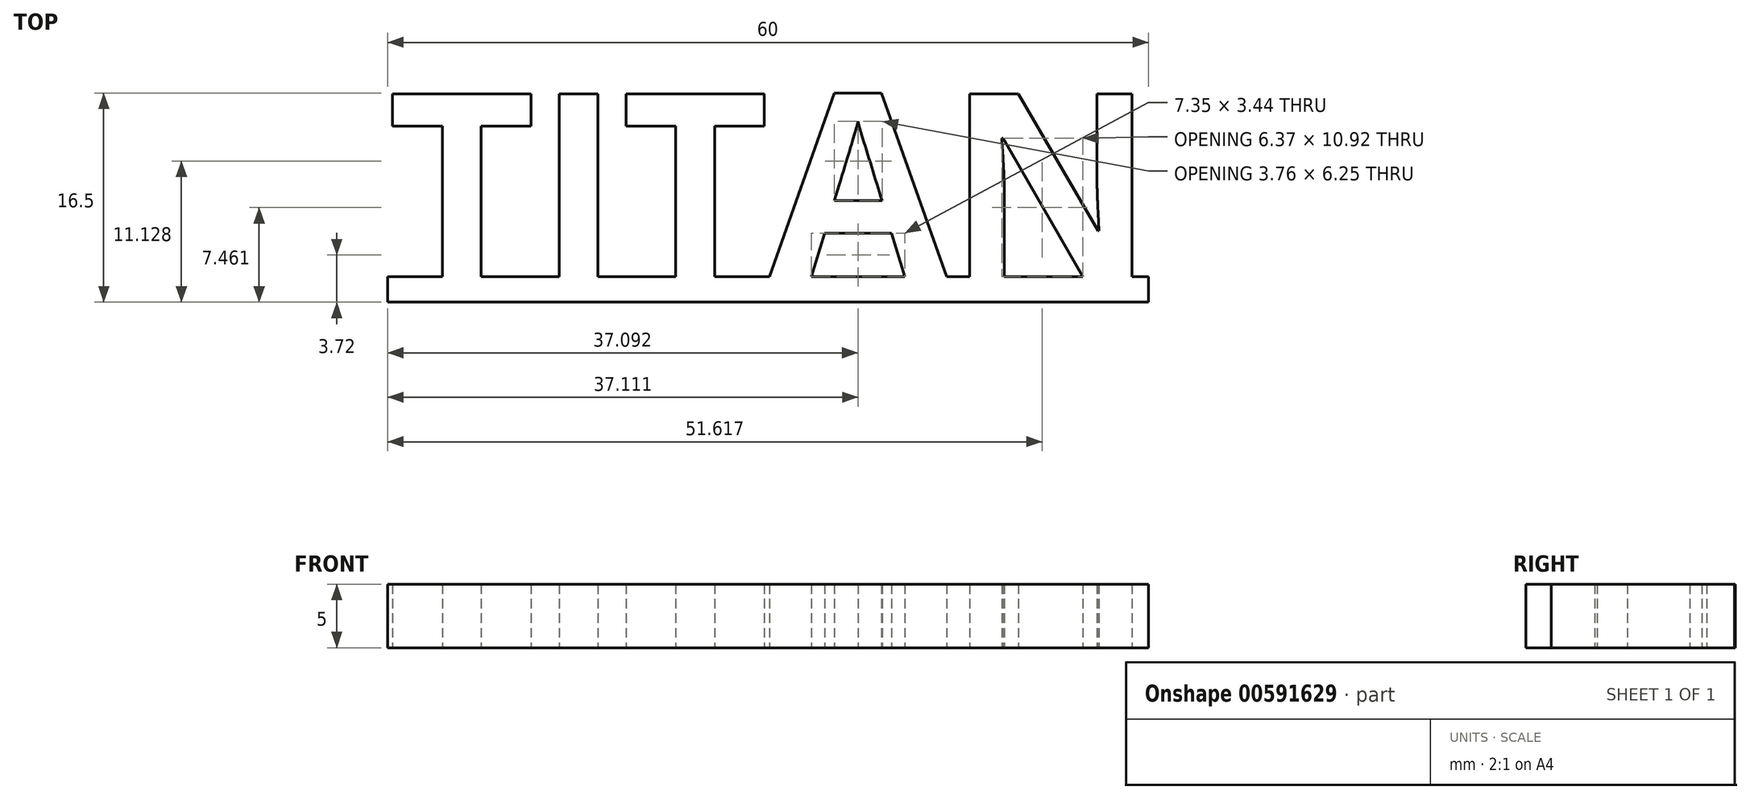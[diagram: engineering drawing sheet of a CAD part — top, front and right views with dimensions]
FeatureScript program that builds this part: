
annotation { "Feature Type Name" : "Feature", "Feature Type Description" : "" }
export const myFeature = defineFeature(function(context is Context, id is Id, definition is map)
    precondition{}
    {
        {
            var Q0;
            Q0=qCreatedBy(makeId("Top.planeOp"),FACE);
            var sketch = newSketch(context, id + "F0", { "sketchPlane" : qUnion([Q0])});
            skText(sketch, "E0", { "text": "TITAN", "fontName": "OpenSans-Bold.ttf"});
            skLineSegment(sketch, "E1.bottom", {"start": v(9.51, -3.08) * mm, "end": v(69.51, -3.08) * mm});
            skLineSegment(sketch, "E1.top", {"start": v(9.51, -5.08) * mm, "end": v(69.51, -5.08) * mm});
            skLineSegment(sketch, "E1.left", {"start": v(9.51, -3.08) * mm, "end": v(9.51, -5.08) * mm});
            skLineSegment(sketch, "E1.right", {"start": v(69.51, -3.08) * mm, "end": v(69.51, -5.08) * mm});
            const initialGuessF0  = {"E0": [0.00951, -0.00308, 1, 0, 0.01456]};
            skSetInitialGuess(sketch, initialGuessF0);
            skSolve(sketch);
        }
        {
            var Q0;
            Q0 = qSketchRegion(id + "F0", true);
            extrude(context, id + "F1", {"entities" : qUnion([Q0]), "depth" : 5 * mm, "offsetDistance" : 25 * mm});
        }
    });
